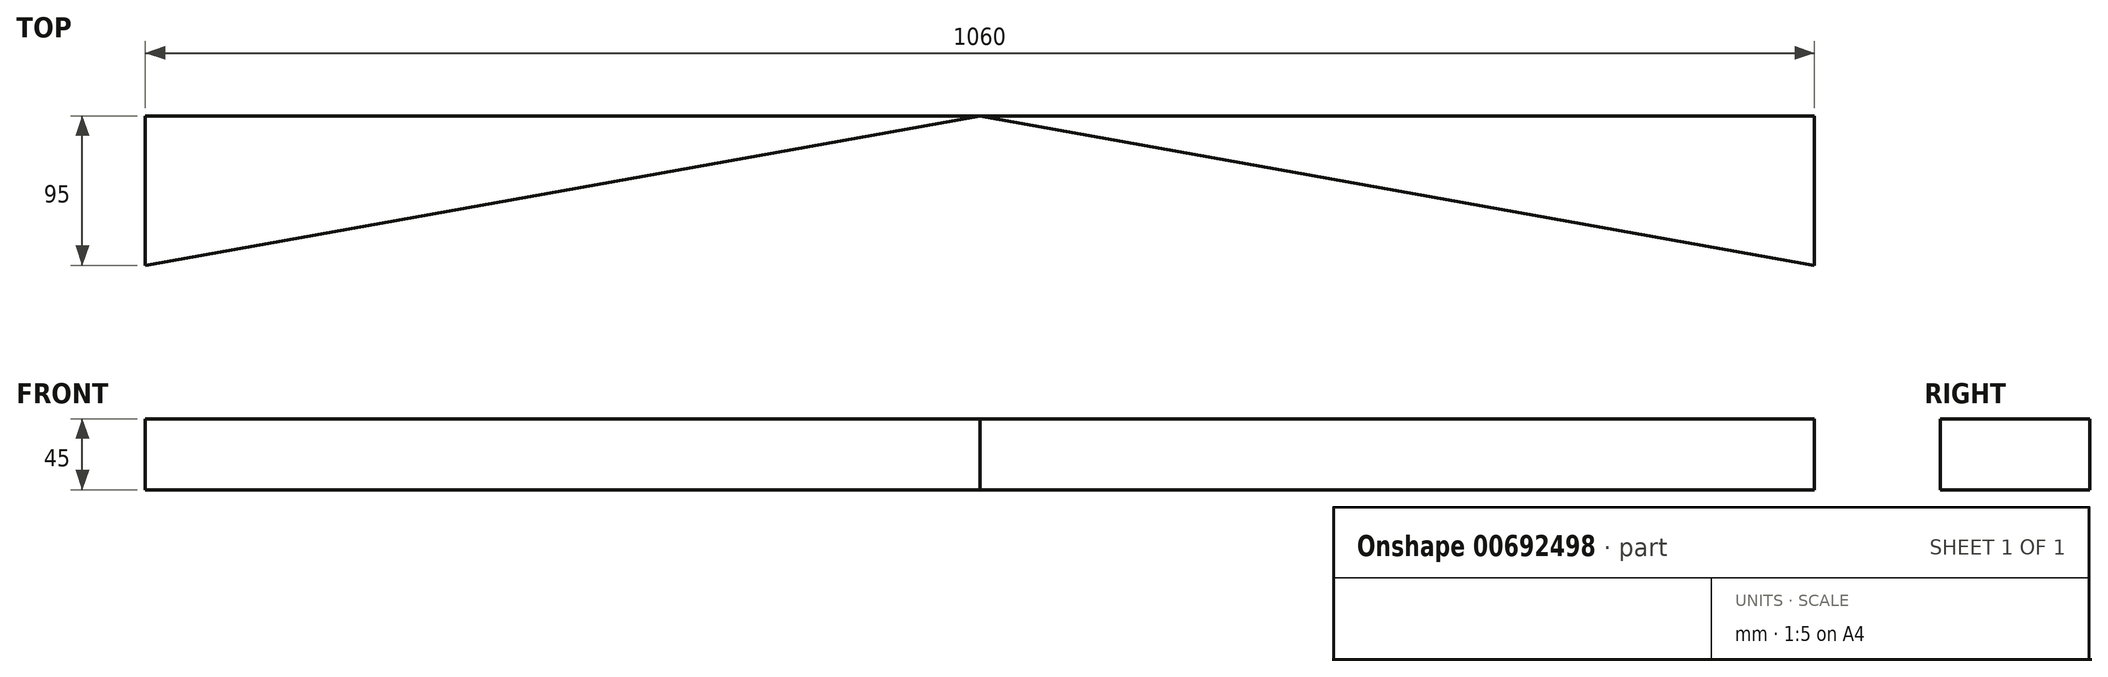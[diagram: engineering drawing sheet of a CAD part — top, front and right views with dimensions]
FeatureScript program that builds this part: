
annotation { "Feature Type Name" : "Feature", "Feature Type Description" : "" }
export const myFeature = defineFeature(function(context is Context, id is Id, definition is map)
    precondition{}
    {
        {
            var Q0;
            Q0=qCreatedBy(makeId("Top.planeOp"),FACE);
            var sketch = newSketch(context, id + "F0", { "sketchPlane" : qUnion([Q0])});
            skLineSegment(sketch, "E0.left", {"start": v(-526.77, -178.52) * mm, "end": v(-526.77, -273.52) * mm});
            skLineSegment(sketch, "E0.right", {"start": v(533.23, -178.52) * mm, "end": v(533.23, -273.52) * mm});
            skLineSegment(sketch, "E1", {"start": v(533.23, -178.52) * mm, "end": v(-526.77, -178.52) * mm});
            skPoint(sketch, "E2", {"position": v(3.23, -178.52) * mm});
            skLineSegment(sketch, "E3", {"start": v(-526.77, -273.52) * mm, "end": v(3.23, -178.52) * mm});
            skLineSegment(sketch, "E4", {"start": v(533.23, -273.52) * mm, "end": v(3.23, -178.52) * mm});
            skSolve(sketch);
        }
        {
            var Q0;
            {var subQ0=sQuery(id+"F0.wireOp",EDGE,"E0.left");Q0=makeQuery(id+"F0.imprint","IMPRINT",FACE,{"disambiguationData":[TD([[makeQuery(id+"F0.imprint","IMPRINT",EDGE,{"derivedFrom":subQ0}),1.0]])]});}
            var Q1;
            {var subQ0=sQuery(id+"F0.wireOp",EDGE,"E0.right");Q1=makeQuery(id+"F0.imprint","IMPRINT",FACE,{"disambiguationData":[TD([[makeQuery(id+"F0.imprint","IMPRINT",EDGE,{"derivedFrom":subQ0}),-1.0]])]});}
            extrude(context, id + "F1", {"entities" : qUnion([Q0, Q1]), "depth" : 45 * mm, "offsetDistance" : 25.4 * mm});
        }
    });
